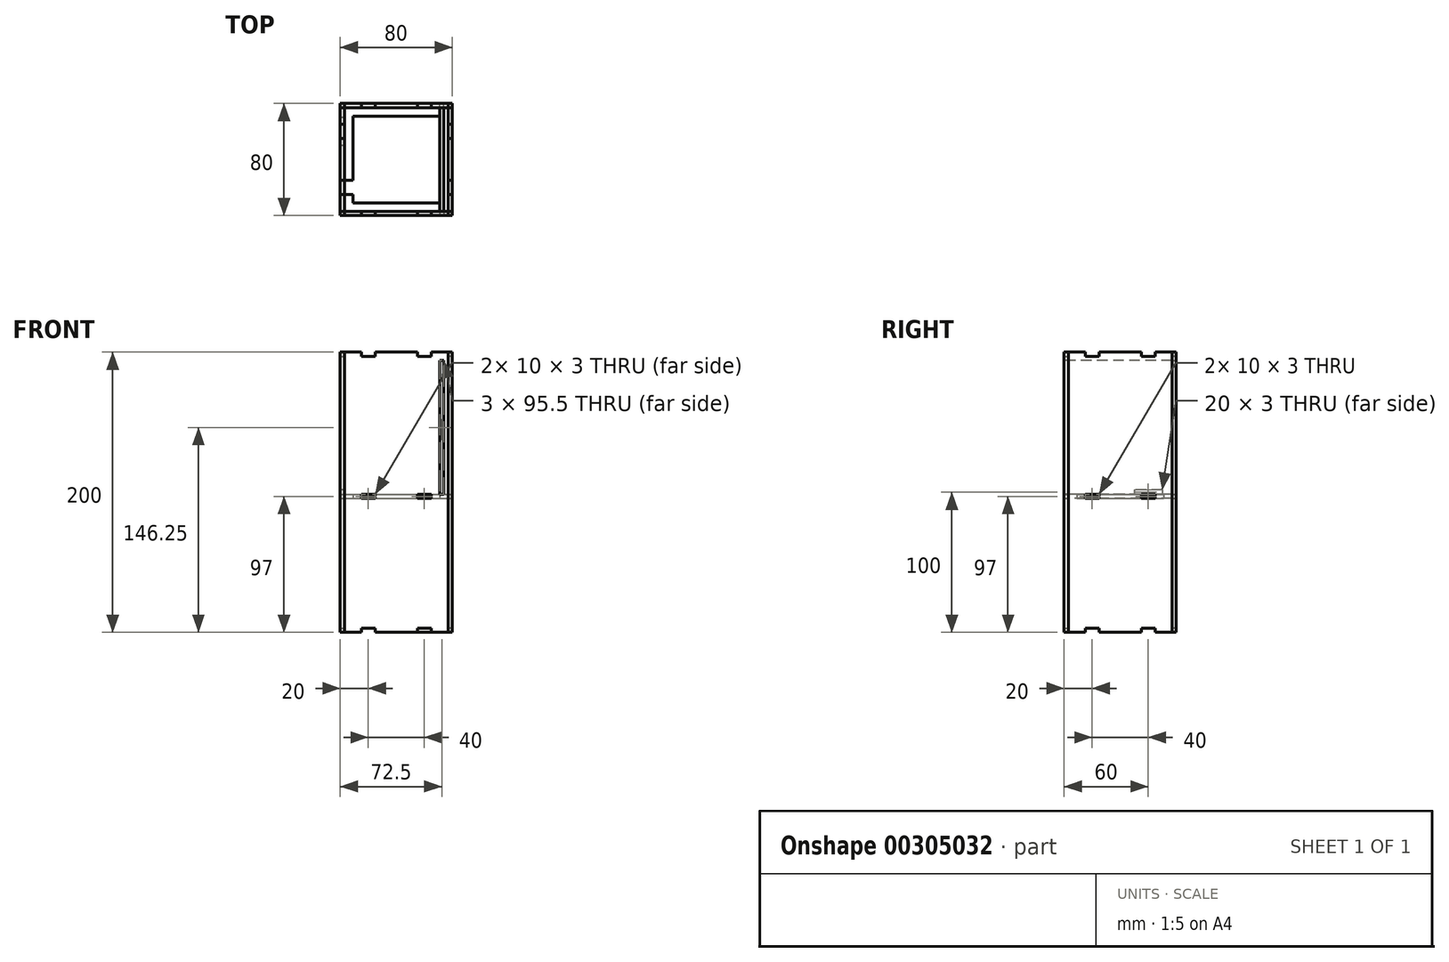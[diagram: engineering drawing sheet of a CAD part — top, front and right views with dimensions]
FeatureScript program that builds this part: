
annotation { "Feature Type Name" : "Feature", "Feature Type Description" : "" }
export const myFeature = defineFeature(function(context is Context, id is Id, definition is map)
    precondition{}
    {
        {
            assignVariable(context, id + "F0", {"name" : "WT", "anyValue" : 3});
        }
        {
            assignVariable(context, id + "F1", {"name" : "BW", "anyValue" : 80});
        }
        {
            assignVariable(context, id + "F2", {"name" : "BL", "anyValue" : 200});
        }
        {
            var Q0;
            Q0=qCreatedBy(makeId("Top.planeOp"),FACE);
            var sketch = newSketch(context, id + "F3", { "sketchPlane" : qUnion([Q0])});
            skLineSegment(sketch, "E0.bottom", {"start": v(-40, 40) * mm, "end": v(40, 40) * mm});
            skLineSegment(sketch, "E0.top", {"start": v(-40, -40) * mm, "end": v(40, -40) * mm});
            skLineSegment(sketch, "E0.left", {"start": v(-40, 40) * mm, "end": v(-40, -40) * mm});
            skLineSegment(sketch, "E0.right", {"start": v(40, 40) * mm, "end": v(40, -40) * mm});
            skPoint(sketch, "E0.middle", {"position": v(0, 0) * mm});
            skLineSegment(sketch, "E1.bottom", {"start": v(-37, 37) * mm, "end": v(37, 37) * mm});
            skLineSegment(sketch, "E1.top", {"start": v(-37, -37) * mm, "end": v(37, -37) * mm});
            skLineSegment(sketch, "E1.left", {"start": v(-37, 37) * mm, "end": v(-37, -37) * mm});
            skLineSegment(sketch, "E1.right", {"start": v(37, 37) * mm, "end": v(37, -37) * mm});
            skCircle(sketch, "E2", {"center": v(0, 0) * mm, "radius": 25 * mm});
            skLineSegment(sketch, "E3", {"start": v(37, 0) * mm, "end": v(40, 0) * mm, "construction": true});
            skLineSegment(sketch, "E4", {"start": v(37, 0) * mm, "end": v(40, 40) * mm, "construction": true});
            skLineSegment(sketch, "E5", {"start": v(0, 37) * mm, "end": v(0, 40) * mm, "construction": true});
            skLineSegment(sketch, "E6", {"start": v(0, 37) * mm, "end": v(40, 40) * mm, "construction": true});
            skLineSegment(sketch, "E7.bottom", {"start": v(25, 40) * mm, "end": v(15, 40) * mm});
            skLineSegment(sketch, "E7.top", {"start": v(25, 37) * mm, "end": v(15, 37) * mm});
            skLineSegment(sketch, "E7.left", {"start": v(25, 40) * mm, "end": v(25, 37) * mm});
            skLineSegment(sketch, "E7.right", {"start": v(15, 40) * mm, "end": v(15, 37) * mm});
            skPoint(sketch, "E7.middle", {"position": v(20, 38.5) * mm});
            skLineSegment(sketch, "E8.bottom", {"start": v(40, 25) * mm, "end": v(37, 25) * mm});
            skLineSegment(sketch, "E8.top", {"start": v(40, 15) * mm, "end": v(37, 15) * mm});
            skLineSegment(sketch, "E8.left", {"start": v(40, 25) * mm, "end": v(40, 15) * mm});
            skLineSegment(sketch, "E8.right", {"start": v(37, 25) * mm, "end": v(37, 15) * mm});
            skPoint(sketch, "E8.middle", {"position": v(38.5, 20) * mm});
            skLineSegment(sketch, "E9.MirrorCS", {"start": v(40, -15) * mm, "end": v(37, -15) * mm});
            skLineSegment(sketch, "E10.MirrorCS", {"start": v(40, -25) * mm, "end": v(37, -25) * mm});
            skLineSegment(sketch, "E11.MirrorCS", {"start": v(-15, 40) * mm, "end": v(-15, 37) * mm});
            skLineSegment(sketch, "E12.MirrorCS", {"start": v(-25, 40) * mm, "end": v(-25, 37) * mm});
            skLineSegment(sketch, "E13.MirrorCS", {"start": v(-40, 25) * mm, "end": v(-37, 25) * mm});
            skLineSegment(sketch, "E14.MirrorCS", {"start": v(-40, 15) * mm, "end": v(-37, 15) * mm});
            skLineSegment(sketch, "E15.MirrorCS", {"start": v(-40, -15) * mm, "end": v(-37, -15) * mm});
            skLineSegment(sketch, "E16.MirrorCS", {"start": v(-40, -25) * mm, "end": v(-37, -25) * mm});
            skLineSegment(sketch, "E17.MirrorCS", {"start": v(15, -40) * mm, "end": v(15, -37) * mm});
            skLineSegment(sketch, "E18.MirrorCS", {"start": v(25, -40) * mm, "end": v(25, -37) * mm});
            skLineSegment(sketch, "E19.MirrorCS", {"start": v(-15, -40) * mm, "end": v(-15, -37) * mm});
            skLineSegment(sketch, "E20.MirrorCS", {"start": v(-25, -40) * mm, "end": v(-25, -37) * mm});
            skSolve(sketch);
        }
        {
            var Q0;
            Q0=qCreatedBy(makeId("Front.planeOp"),FACE);
            cPlane(context, id + "F4", {"entities" : qUnion([Q0]), "cplaneType" : CPlaneType.OFFSET, "offset" : getVariable(context, 'BW') / 2 * mm, "width" : 150 * mm, "height" : 150 * mm});
        }
        {
            var Q0;
            Q0=qCreatedBy(id+"F4.planeOp",FACE);
            var sketch = newSketch(context, id + "F5", { "sketchPlane" : qUnion([Q0])});
            skLineSegment(sketch, "E21.0", {"start": v(-40, 0) * mm, "end": v(40, 0) * mm});
            skLineSegment(sketch, "E22", {"start": v(-40, 0) * mm, "end": v(-40, 200) * mm});
            skLineSegment(sketch, "E23.MirrorCS", {"start": v(40, 0) * mm, "end": v(40, 200) * mm});
            skLineSegment(sketch, "E24", {"start": v(-40, 100) * mm, "end": v(40, 100) * mm, "construction": true});
            skLineSegment(sketch, "E25.MirrorCS", {"start": v(-40, 200) * mm, "end": v(40, 200) * mm});
            skLineSegment(sketch, "E26.bottom", {"start": v(-37, 197) * mm, "end": v(37, 197) * mm});
            skLineSegment(sketch, "E26.top", {"start": v(-37, 3) * mm, "end": v(37, 3) * mm});
            skLineSegment(sketch, "E26.left", {"start": v(-37, 197) * mm, "end": v(-37, 3) * mm});
            skLineSegment(sketch, "E26.right", {"start": v(37, 197) * mm, "end": v(37, 3) * mm});
            skPoint(sketch, "E26.middle", {"position": v(0, 100) * mm});
            skLineSegment(sketch, "E27", {"start": v(-40, 101.5) * mm, "end": v(-37, 101.5) * mm});
            skLineSegment(sketch, "E28", {"start": v(-40, 98.5) * mm, "end": v(-37, 98.5) * mm});
            skLineSegment(sketch, "E29", {"start": v(-37, 98.5) * mm, "end": v(-34, 98.5) * mm});
            skLineSegment(sketch, "E30", {"start": v(-34, 98.5) * mm, "end": v(-34, 194) * mm});
            skLineSegment(sketch, "E31", {"start": v(0, 100) * mm, "end": v(0, 148.42) * mm, "construction": true});
            skLineSegment(sketch, "E32", {"start": v(-31, 95.5) * mm, "end": v(-31, 194) * mm});
            skLineSegment(sketch, "E33", {"start": v(-34, 194) * mm, "end": v(-31, 194) * mm});
            skLineSegment(sketch, "E34", {"start": v(-31, 95.5) * mm, "end": v(-37, 95.5) * mm});
            skLineSegment(sketch, "E35.MirrorCS", {"start": v(31, 95.5) * mm, "end": v(31, 194) * mm});
            skLineSegment(sketch, "E36.MirrorCS", {"start": v(31, 95.5) * mm, "end": v(37, 95.5) * mm});
            skLineSegment(sketch, "E37.MirrorCS", {"start": v(34, 98.5) * mm, "end": v(34, 194) * mm});
            skLineSegment(sketch, "E38.MirrorCS", {"start": v(34, 194) * mm, "end": v(31, 194) * mm});
            skLineSegment(sketch, "E39.MirrorCS", {"start": v(37, 98.5) * mm, "end": v(34, 98.5) * mm});
            skLineSegment(sketch, "E40.MirrorCS", {"start": v(40, 98.5) * mm, "end": v(37, 98.5) * mm});
            skLineSegment(sketch, "E41.MirrorCS", {"start": v(40, 101.5) * mm, "end": v(37, 101.5) * mm});
            skLineSegment(sketch, "E42", {"start": v(-34, 98.5) * mm, "end": v(-31, 98.5) * mm});
            skLineSegment(sketch, "E43", {"start": v(34, 98.5) * mm, "end": v(31, 98.5) * mm});
            skSolve(sketch);
        }
        {
            var Q0;
            Q0=qCreatedBy(id+"F4.planeOp",FACE);
            var sketch = newSketch(context, id + "F6", { "sketchPlane" : qUnion([Q0])});
            skLineSegment(sketch, "E44.0", {"start": v(-40, 200) * mm, "end": v(40, 200) * mm});
            skLineSegment(sketch, "E45.0", {"start": v(40, 0) * mm, "end": v(40, 200) * mm});
            skLineSegment(sketch, "E46.0", {"start": v(-40, 0) * mm, "end": v(-40, 200) * mm});
            skLineSegment(sketch, "E47.0", {"start": v(-40, 0) * mm, "end": v(40, 0) * mm});
            skSolve(sketch);
        }
        {
            var Q0;
            Q0=qCreatedBy(makeId("Front.planeOp"),FACE);
            cPlane(context, id + "F7", {"entities" : qUnion([Q0]), "cplaneType" : CPlaneType.OFFSET, "offset" : (getVariable(context, 'BW') / 2) * mm, "oppositeDirection" : true, "width" : 150 * mm, "height" : 150 * mm});
        }
        {
            var Q0;
            Q0=qCreatedBy(id+"F7.planeOp",FACE);
            var sketch = newSketch(context, id + "F8", { "sketchPlane" : qUnion([Q0])});
            skLineSegment(sketch, "E48.0", {"start": v(-40, 0) * mm, "end": v(-40, 200) * mm});
            skLineSegment(sketch, "E49.0", {"start": v(-40, 200) * mm, "end": v(40, 200) * mm});
            skLineSegment(sketch, "E50.0", {"start": v(40, 0) * mm, "end": v(40, 200) * mm});
            skLineSegment(sketch, "E51.0", {"start": v(-40, 0) * mm, "end": v(40, 0) * mm});
            skLineSegment(sketch, "E52.0", {"start": v(-37, 197) * mm, "end": v(-37, 3) * mm});
            skLineSegment(sketch, "E53.0", {"start": v(37, 197) * mm, "end": v(37, 3) * mm});
            skLineSegment(sketch, "E54.0", {"start": v(-37, 197) * mm, "end": v(37, 197) * mm});
            skLineSegment(sketch, "E55.0", {"start": v(-37, 3) * mm, "end": v(37, 3) * mm});
            skSolve(sketch);
        }
        {
            var Q0;
            Q0=qCreatedBy(makeId("Top.planeOp"),FACE);
            cPlane(context, id + "F9", {"entities" : qUnion([Q0]), "cplaneType" : CPlaneType.OFFSET, "offset" : (getVariable(context, 'BL')) * mm, "width" : 150 * mm, "height" : 150 * mm});
        }
        {
            var Q0;
            Q0=qCreatedBy(id+"F9.planeOp",FACE);
            var sketch = newSketch(context, id + "F10", { "sketchPlane" : qUnion([Q0])});
            skLineSegment(sketch, "E56.0", {"start": v(-40, 40) * mm, "end": v(-40, -40) * mm});
            skLineSegment(sketch, "E57.0", {"start": v(-40, 40) * mm, "end": v(40, 40) * mm});
            skLineSegment(sketch, "E58.0", {"start": v(40, 40) * mm, "end": v(40, -40) * mm});
            skLineSegment(sketch, "E59.0", {"start": v(-40, -40) * mm, "end": v(40, -40) * mm});
            skLineSegment(sketch, "E60.0", {"start": v(-37, -37) * mm, "end": v(37, -37) * mm});
            skLineSegment(sketch, "E61.0", {"start": v(-37, 37) * mm, "end": v(-37, -37) * mm});
            skLineSegment(sketch, "E62.0", {"start": v(37, 37) * mm, "end": v(37, -37) * mm});
            skLineSegment(sketch, "E63.0", {"start": v(-37, 37) * mm, "end": v(37, 37) * mm});
            skLineSegment(sketch, "E64.0", {"start": v(40, -25) * mm, "end": v(37, -25) * mm});
            skLineSegment(sketch, "E65.0", {"start": v(40, -15) * mm, "end": v(37, -15) * mm});
            skLineSegment(sketch, "E65.1", {"start": v(25, -40) * mm, "end": v(25, -37) * mm});
            skLineSegment(sketch, "E65.2", {"start": v(15, -40) * mm, "end": v(15, -37) * mm});
            skLineSegment(sketch, "E65.3", {"start": v(-15, -40) * mm, "end": v(-15, -37) * mm});
            skLineSegment(sketch, "E65.4", {"start": v(-25, -40) * mm, "end": v(-25, -37) * mm});
            skLineSegment(sketch, "E65.5", {"start": v(-40, -25) * mm, "end": v(-37, -25) * mm});
            skLineSegment(sketch, "E65.6", {"start": v(-40, -15) * mm, "end": v(-37, -15) * mm});
            skLineSegment(sketch, "E65.7", {"start": v(-40, 15) * mm, "end": v(-37, 15) * mm});
            skLineSegment(sketch, "E65.8", {"start": v(-40, 25) * mm, "end": v(-37, 25) * mm});
            skLineSegment(sketch, "E65.9", {"start": v(-25, 40) * mm, "end": v(-25, 37) * mm});
            skLineSegment(sketch, "E65.10", {"start": v(-15, 40) * mm, "end": v(-15, 37) * mm});
            skLineSegment(sketch, "E65.11", {"start": v(15, 40) * mm, "end": v(15, 37) * mm});
            skLineSegment(sketch, "E65.12", {"start": v(25, 40) * mm, "end": v(25, 37) * mm});
            skLineSegment(sketch, "E65.13", {"start": v(40, 25) * mm, "end": v(37, 25) * mm});
            skLineSegment(sketch, "E65.14", {"start": v(40, 15) * mm, "end": v(37, 15) * mm});
            skCircle(sketch, "E66.0", {"center": v(0, 0) * mm, "radius": 25 * mm});
            skSolve(sketch);
        }
        {
            var Q0;
            Q0=qCreatedBy(makeId("Right.planeOp"),FACE);
            cPlane(context, id + "F11", {"entities" : qUnion([Q0]), "cplaneType" : CPlaneType.OFFSET, "offset" : (getVariable(context, 'BW') / 2) * mm, "width" : 150 * mm, "height" : 150 * mm});
        }
        {
            var Q0;
            Q0=qCreatedBy(id+"F11.planeOp",FACE);
            var sketch = newSketch(context, id + "F12", { "sketchPlane" : qUnion([Q0])});
            skLineSegment(sketch, "E67.0", {"start": v(-40, 0) * mm, "end": v(-40, 200) * mm});
            skLineSegment(sketch, "E68.0", {"start": v(40, 200) * mm, "end": v(-40, 200) * mm});
            skLineSegment(sketch, "E69.0", {"start": v(40, 0) * mm, "end": v(40, 200) * mm});
            skLineSegment(sketch, "E70.0", {"start": v(40, 0) * mm, "end": v(-40, 0) * mm});
            skSolve(sketch);
        }
        {
            var Q0;
            Q0=qCreatedBy(makeId("Right.planeOp"),FACE);
            cPlane(context, id + "F13", {"entities" : qUnion([Q0]), "cplaneType" : CPlaneType.OFFSET, "offset" : (getVariable(context, 'BW') / 2) * mm, "oppositeDirection" : true, "width" : 150 * mm, "height" : 150 * mm});
        }
        {
            var Q0;
            Q0=qCreatedBy(id+"F13.planeOp",FACE);
            var sketch = newSketch(context, id + "F14", { "sketchPlane" : qUnion([Q0])});
            skLineSegment(sketch, "E71.0", {"start": v(40, 0) * mm, "end": v(40, 200) * mm});
            skLineSegment(sketch, "E72.0", {"start": v(-40, 0) * mm, "end": v(-40, 200) * mm});
            skLineSegment(sketch, "E73.0", {"start": v(40, 200) * mm, "end": v(-40, 200) * mm});
            skLineSegment(sketch, "E74.0", {"start": v(40, 0) * mm, "end": v(-40, 0) * mm});
            skLineSegment(sketch, "E75", {"start": v(40, 100) * mm, "end": v(-40, 100) * mm, "construction": true});
            skLineSegment(sketch, "E76", {"start": v(0, 100) * mm, "end": v(0, 101.5) * mm, "construction": true});
            skPoint(sketch, "E76.endSnap0", {"position": v(0, 100) * mm});
            skLineSegment(sketch, "E77", {"start": v(0, 100) * mm, "end": v(0, 98.5) * mm, "construction": true});
            skLineSegment(sketch, "E78", {"start": v(0, 101.5) * mm, "end": v(40, 101.5) * mm, "construction": true});
            skLineSegment(sketch, "E79", {"start": v(40, 101.5) * mm, "end": v(0, 98.5) * mm, "construction": true});
            skLineSegment(sketch, "E80.bottom", {"start": v(30, 101.5) * mm, "end": v(10, 101.5) * mm});
            skLineSegment(sketch, "E80.top", {"start": v(30, 98.5) * mm, "end": v(10, 98.5) * mm});
            skLineSegment(sketch, "E80.left", {"start": v(30, 101.5) * mm, "end": v(30, 98.5) * mm});
            skLineSegment(sketch, "E80.right", {"start": v(10, 101.5) * mm, "end": v(10, 98.5) * mm});
            skPoint(sketch, "E80.middle", {"position": v(20, 100) * mm});
            skSolve(sketch);
        }
        {
            var Q0;
            Q0=makeQuery(id+"F5.imprint","IMPRINT",FACE,{"disambiguationData":[TD([[makeQuery(id+"F5.imprint","IMPRINT",EDGE,{"derivedFrom":sQuery(id+"F5.wireOp",EDGE,"E35.MirrorCS")}),-1.0]])]});
            extrude(context, id + "F15", {"entities" : qUnion([Q0]), "oppositeDirection" : true, "depth" : (getVariable(context, 'BW')) * mm});
        }
        {
            var Q0;
            Q0=sQuery(id+"F5.wireOp",EDGE,"E34");
            cPlane(context, id + "F16", {"entities" : qUnion([Q0]), "cplaneType" : CPlaneType.LINE_ANGLE, "offset" : 25 * mm, "angle" : 90 * degree, "width" : 150 * mm, "height" : 150 * mm});
        }
        {
            var Q0;
            Q0=qCreatedBy(id+"F16.planeOp",FACE);
            var sketch = newSketch(context, id + "F17", { "sketchPlane" : qUnion([Q0])});
            skLineSegment(sketch, "E81.0", {"start": v(-40, 40) * mm, "end": v(-40, -40) * mm});
            skLineSegment(sketch, "E82.0", {"start": v(-40, -40) * mm, "end": v(40, -40) * mm});
            skLineSegment(sketch, "E83.0", {"start": v(40, 40) * mm, "end": v(40, -40) * mm});
            skLineSegment(sketch, "E84.0", {"start": v(-40, 40) * mm, "end": v(40, 40) * mm});
            skLineSegment(sketch, "E85.bottom", {"start": v(-31, -31) * mm, "end": v(31, -31) * mm});
            skLineSegment(sketch, "E85.top", {"start": v(-31, 31) * mm, "end": v(31, 31) * mm});
            skLineSegment(sketch, "E85.left", {"start": v(-31, -31) * mm, "end": v(-31, 31) * mm});
            skLineSegment(sketch, "E85.right", {"start": v(31, -31) * mm, "end": v(31, 31) * mm});
            skPoint(sketch, "E85.middle", {"position": v(0, 0) * mm});
            skLineSegment(sketch, "E86", {"start": v(0, -31) * mm, "end": v(0, -40) * mm, "construction": true});
            skLineSegment(sketch, "E87", {"start": v(-31, 0) * mm, "end": v(-40, 0) * mm, "construction": true});
            skLineSegment(sketch, "E88", {"start": v(-31, 0) * mm, "end": v(-40, -40) * mm, "construction": true});
            skLineSegment(sketch, "E89", {"start": v(-40, -40) * mm, "end": v(0, -31) * mm, "construction": true});
            skLineSegment(sketch, "E90.bottom", {"start": v(-25, -40) * mm, "end": v(-15, -40) * mm, "construction": true});
            skLineSegment(sketch, "E90.top", {"start": v(-25, -31) * mm, "end": v(-15, -31) * mm, "construction": true});
            skLineSegment(sketch, "E90.left", {"start": v(-25, -40) * mm, "end": v(-25, -31) * mm});
            skLineSegment(sketch, "E90.right", {"start": v(-15, -40) * mm, "end": v(-15, -31) * mm});
            skPoint(sketch, "E90.middle", {"position": v(-20, -35.5) * mm});
            skLineSegment(sketch, "E91.bottom", {"start": v(-40, -25) * mm, "end": v(-31, -25) * mm});
            skLineSegment(sketch, "E91.top", {"start": v(-40, -15) * mm, "end": v(-31, -15) * mm});
            skLineSegment(sketch, "E91.left", {"start": v(-40, -25) * mm, "end": v(-40, -15) * mm});
            skLineSegment(sketch, "E91.right", {"start": v(-31, -25) * mm, "end": v(-31, -15) * mm});
            skPoint(sketch, "E91.middle", {"position": v(-35.5, -20) * mm});
            skLineSegment(sketch, "E92.MirrorCS", {"start": v(15, -40) * mm, "end": v(15, -31) * mm});
            skLineSegment(sketch, "E93.MirrorCS", {"start": v(25, -40) * mm, "end": v(25, -31) * mm});
            skLineSegment(sketch, "E94.MirrorCS", {"start": v(-40, 15) * mm, "end": v(-31, 15) * mm});
            skLineSegment(sketch, "E95.MirrorCS", {"start": v(-40, 25) * mm, "end": v(-31, 25) * mm});
            skLineSegment(sketch, "E96.MirrorCS", {"start": v(-15, 40) * mm, "end": v(-15, 31) * mm});
            skLineSegment(sketch, "E97.MirrorCS", {"start": v(-25, 40) * mm, "end": v(-25, 31) * mm});
            skLineSegment(sketch, "E98.MirrorCS", {"start": v(15, 40) * mm, "end": v(15, 31) * mm});
            skLineSegment(sketch, "E99.MirrorCS", {"start": v(25, 40) * mm, "end": v(25, 31) * mm});
            skLineSegment(sketch, "E100.MirrorCS", {"start": v(40, -25) * mm, "end": v(31, -25) * mm});
            skLineSegment(sketch, "E101.MirrorCS", {"start": v(40, -15) * mm, "end": v(31, -15) * mm});
            skLineSegment(sketch, "E102.MirrorCS", {"start": v(40, 15) * mm, "end": v(31, 15) * mm});
            skLineSegment(sketch, "E103.MirrorCS", {"start": v(40, 25) * mm, "end": v(31, 25) * mm});
            skLineSegment(sketch, "E104.0", {"start": v(-37, 37) * mm, "end": v(37, 37) * mm});
            skLineSegment(sketch, "E105.0", {"start": v(37, 37) * mm, "end": v(37, -37) * mm});
            skLineSegment(sketch, "E106.0", {"start": v(-37, -37) * mm, "end": v(37, -37) * mm});
            skLineSegment(sketch, "E107.0", {"start": v(-37, 37) * mm, "end": v(-37, -37) * mm});
            skSolve(sketch);
        }
        {
            var Q0;
            {var subQ0=sQuery(id+"F17.wireOp",EDGE,"E96.MirrorCS");var subQ1=sQuery(id+"F17.wireOp",EDGE,"E85.top");var subQ2=makeQuery(id+"F17.imprint","INTERSECT",VERTEX,{"derivedFrom":[subQ1,subQ0]});Q0=makeQuery(id+"F17.imprint","IMPRINT",FACE,{"disambiguationData":[TD([[makeQuery(id+"F17.imprint","IMPRINT",EDGE,{"disambiguationData":[TD([[subQ2,1.0]])],"derivedFrom":subQ1}),1.0]])]});}
            var Q1;
            {var subQ0=sQuery(id+"F17.wireOp",EDGE,"E96.MirrorCS");var subQ1=sQuery(id+"F17.wireOp",EDGE,"E84.0");var subQ2=makeQuery(id+"F17.imprint","INTERSECT",VERTEX,{"derivedFrom":[subQ1,subQ0]});Q1=makeQuery(id+"F17.imprint","IMPRINT",FACE,{"disambiguationData":[TD([[makeQuery(id+"F17.imprint","IMPRINT",EDGE,{"disambiguationData":[TD([[subQ2,1.0]])],"derivedFrom":subQ1}),-1.0]])]});}
            var Q2;
            {var subQ0=sQuery(id+"F17.wireOp",EDGE,"E96.MirrorCS");var subQ1=sQuery(id+"F17.wireOp",EDGE,"E85.top");var subQ2=makeQuery(id+"F17.imprint","INTERSECT",VERTEX,{"derivedFrom":[subQ1,subQ0]});Q2=makeQuery(id+"F17.imprint","IMPRINT",FACE,{"disambiguationData":[TD([[makeQuery(id+"F17.imprint","IMPRINT",EDGE,{"disambiguationData":[TD([[subQ2,-1.0]])],"derivedFrom":subQ1}),1.0]])]});}
            var Q3;
            {var subQ1=sQuery(id+"F17.wireOp",EDGE,"E85.left");var subQ5=sQuery(id+"F17.wireOp",EDGE,"E85.top");var subQ6=makeQuery(id+"F17.imprint","INTERSECT",VERTEX,{"derivedFrom":[subQ5,subQ1]});Q3=makeQuery(id+"F17.imprint","IMPRINT",FACE,{"disambiguationData":[TD([[makeQuery(id+"F17.imprint","IMPRINT",EDGE,{"disambiguationData":[TD([[subQ6,-1.0]])],"derivedFrom":subQ5}),1.0]])]});}
            var Q4;
            {var subQ0=sQuery(id+"F17.wireOp",EDGE,"E98.MirrorCS");var subQ1=sQuery(id+"F17.wireOp",EDGE,"E85.top");var subQ2=makeQuery(id+"F17.imprint","INTERSECT",VERTEX,{"derivedFrom":[subQ1,subQ0]});Q4=makeQuery(id+"F17.imprint","IMPRINT",FACE,{"disambiguationData":[TD([[makeQuery(id+"F17.imprint","IMPRINT",EDGE,{"disambiguationData":[TD([[subQ2,-1.0]])],"derivedFrom":subQ1}),1.0]])]});}
            var Q5;
            {var subQ0=sQuery(id+"F17.wireOp",EDGE,"E98.MirrorCS");var subQ1=sQuery(id+"F17.wireOp",EDGE,"E84.0");var subQ2=makeQuery(id+"F17.imprint","INTERSECT",VERTEX,{"derivedFrom":[subQ1,subQ0]});Q5=makeQuery(id+"F17.imprint","IMPRINT",FACE,{"disambiguationData":[TD([[makeQuery(id+"F17.imprint","IMPRINT",EDGE,{"disambiguationData":[TD([[subQ2,-1.0]])],"derivedFrom":subQ1}),-1.0]])]});}
            var Q6;
            {var subQ1=sQuery(id+"F17.wireOp",EDGE,"E85.right");var subQ5=sQuery(id+"F17.wireOp",EDGE,"E85.top");var subQ6=makeQuery(id+"F17.imprint","INTERSECT",VERTEX,{"derivedFrom":[subQ5,subQ1]});Q6=makeQuery(id+"F17.imprint","IMPRINT",FACE,{"disambiguationData":[TD([[makeQuery(id+"F17.imprint","IMPRINT",EDGE,{"disambiguationData":[TD([[subQ6,1.0]])],"derivedFrom":subQ5}),1.0]])]});}
            var Q7;
            {var subQ0=sQuery(id+"F17.wireOp",EDGE,"E102.MirrorCS");var subQ1=sQuery(id+"F17.wireOp",EDGE,"E85.right");var subQ2=makeQuery(id+"F17.imprint","INTERSECT",VERTEX,{"derivedFrom":[subQ1,subQ0]});Q7=makeQuery(id+"F17.imprint","IMPRINT",FACE,{"disambiguationData":[TD([[makeQuery(id+"F17.imprint","IMPRINT",EDGE,{"disambiguationData":[TD([[subQ2,-1.0]])],"derivedFrom":subQ1}),-1.0]])]});}
            var Q8;
            {var subQ0=sQuery(id+"F17.wireOp",EDGE,"E102.MirrorCS");var subQ1=sQuery(id+"F17.wireOp",EDGE,"E83.0");var subQ2=makeQuery(id+"F17.imprint","INTERSECT",VERTEX,{"derivedFrom":[subQ1,subQ0]});Q8=makeQuery(id+"F17.imprint","IMPRINT",FACE,{"disambiguationData":[TD([[makeQuery(id+"F17.imprint","IMPRINT",EDGE,{"disambiguationData":[TD([[subQ2,1.0]])],"derivedFrom":subQ1}),-1.0]])]});}
            var Q9;
            {var subQ0=sQuery(id+"F17.wireOp",EDGE,"E94.MirrorCS");var subQ1=sQuery(id+"F17.wireOp",EDGE,"E81.0");var subQ2=makeQuery(id+"F17.imprint","INTERSECT",VERTEX,{"derivedFrom":[subQ1,subQ0]});Q9=makeQuery(id+"F17.imprint","IMPRINT",FACE,{"disambiguationData":[TD([[makeQuery(id+"F17.imprint","IMPRINT",EDGE,{"disambiguationData":[TD([[subQ2,1.0]])],"derivedFrom":subQ1}),1.0]])]});}
            var Q10;
            {var subQ0=sQuery(id+"F17.wireOp",EDGE,"E94.MirrorCS");var subQ1=sQuery(id+"F17.wireOp",EDGE,"E85.left");var subQ2=makeQuery(id+"F17.imprint","INTERSECT",VERTEX,{"derivedFrom":[subQ1,subQ0]});Q10=makeQuery(id+"F17.imprint","IMPRINT",FACE,{"disambiguationData":[TD([[makeQuery(id+"F17.imprint","IMPRINT",EDGE,{"disambiguationData":[TD([[subQ2,-1.0]])],"derivedFrom":subQ1}),1.0]])]});}
            var Q11;
            {var subQ1=sQuery(id+"F17.wireOp",EDGE,"E85.left");var subQ3=sQuery(id+"F17.wireOp",EDGE,"E94.MirrorCS");var subQ4=makeQuery(id+"F17.imprint","INTERSECT",VERTEX,{"derivedFrom":[subQ1,subQ3]});Q11=makeQuery(id+"F17.imprint","IMPRINT",FACE,{"disambiguationData":[TD([[makeQuery(id+"F17.imprint","IMPRINT",EDGE,{"disambiguationData":[TD([[subQ4,1.0]])],"derivedFrom":subQ3}),-1.0]])]});}
            var Q12;
            {var subQ0=sQuery(id+"F17.wireOp",EDGE,"E101.MirrorCS");var subQ1=sQuery(id+"F17.wireOp",EDGE,"E85.right");var subQ2=makeQuery(id+"F17.imprint","INTERSECT",VERTEX,{"derivedFrom":[subQ1,subQ0]});Q12=makeQuery(id+"F17.imprint","IMPRINT",FACE,{"disambiguationData":[TD([[makeQuery(id+"F17.imprint","IMPRINT",EDGE,{"disambiguationData":[TD([[subQ2,-1.0]])],"derivedFrom":subQ1}),-1.0]])]});}
            var Q13;
            {var subQ0=sQuery(id+"F17.wireOp",EDGE,"E100.MirrorCS");var subQ1=sQuery(id+"F17.wireOp",EDGE,"E85.right");var subQ2=makeQuery(id+"F17.imprint","INTERSECT",VERTEX,{"derivedFrom":[subQ1,subQ0]});Q13=makeQuery(id+"F17.imprint","IMPRINT",FACE,{"disambiguationData":[TD([[makeQuery(id+"F17.imprint","IMPRINT",EDGE,{"disambiguationData":[TD([[subQ2,-1.0]])],"derivedFrom":subQ1}),-1.0]])]});}
            var Q14;
            {var subQ0=sQuery(id+"F17.wireOp",EDGE,"E100.MirrorCS");var subQ1=sQuery(id+"F17.wireOp",EDGE,"E83.0");var subQ2=makeQuery(id+"F17.imprint","INTERSECT",VERTEX,{"derivedFrom":[subQ1,subQ0]});Q14=makeQuery(id+"F17.imprint","IMPRINT",FACE,{"disambiguationData":[TD([[makeQuery(id+"F17.imprint","IMPRINT",EDGE,{"disambiguationData":[TD([[subQ2,1.0]])],"derivedFrom":subQ1}),-1.0]])]});}
            var Q15;
            {var subQ0=sQuery(id+"F17.wireOp",EDGE,"E91.right");Q15=makeQuery(id+"F17.imprint","IMPRINT",FACE,{"disambiguationData":[TD([[makeQuery(id+"F17.imprint","IMPRINT",EDGE,{"derivedFrom":subQ0}),1.0]])]});}
            var Q16;
            {var subQ0=sQuery(id+"F17.wireOp",EDGE,"E91.left");Q16=makeQuery(id+"F17.imprint","IMPRINT",FACE,{"disambiguationData":[TD([[makeQuery(id+"F17.imprint","IMPRINT",EDGE,{"derivedFrom":subQ0}),-1.0]])]});}
            var Q17;
            {var subQ0=sQuery(id+"F17.wireOp",EDGE,"E90.left");var subQ1=sQuery(id+"F17.wireOp",EDGE,"E85.bottom");var subQ2=makeQuery(id+"F17.imprint","INTERSECT",VERTEX,{"derivedFrom":[subQ1,subQ0]});Q17=makeQuery(id+"F17.imprint","IMPRINT",FACE,{"disambiguationData":[TD([[makeQuery(id+"F17.imprint","IMPRINT",EDGE,{"disambiguationData":[TD([[subQ2,-1.0]])],"derivedFrom":subQ1}),-1.0]])]});}
            var Q18;
            {var subQ0=sQuery(id+"F17.wireOp",EDGE,"E90.left");var subQ1=sQuery(id+"F17.wireOp",EDGE,"E82.0");var subQ2=makeQuery(id+"F17.imprint","INTERSECT",VERTEX,{"derivedFrom":[subQ1,subQ0]});Q18=makeQuery(id+"F17.imprint","IMPRINT",FACE,{"disambiguationData":[TD([[makeQuery(id+"F17.imprint","IMPRINT",EDGE,{"disambiguationData":[TD([[subQ2,-1.0]])],"derivedFrom":subQ1}),1.0]])]});}
            var Q19;
            {var subQ0=sQuery(id+"F17.wireOp",EDGE,"E92.MirrorCS");var subQ1=sQuery(id+"F17.wireOp",EDGE,"E82.0");var subQ2=makeQuery(id+"F17.imprint","INTERSECT",VERTEX,{"derivedFrom":[subQ1,subQ0]});Q19=makeQuery(id+"F17.imprint","IMPRINT",FACE,{"disambiguationData":[TD([[makeQuery(id+"F17.imprint","IMPRINT",EDGE,{"disambiguationData":[TD([[subQ2,-1.0]])],"derivedFrom":subQ1}),1.0]])]});}
            var Q20;
            {var subQ0=sQuery(id+"F17.wireOp",EDGE,"E92.MirrorCS");var subQ1=sQuery(id+"F17.wireOp",EDGE,"E85.bottom");var subQ2=makeQuery(id+"F17.imprint","INTERSECT",VERTEX,{"derivedFrom":[subQ1,subQ0]});Q20=makeQuery(id+"F17.imprint","IMPRINT",FACE,{"disambiguationData":[TD([[makeQuery(id+"F17.imprint","IMPRINT",EDGE,{"disambiguationData":[TD([[subQ2,-1.0]])],"derivedFrom":subQ1}),-1.0]])]});}
            var Q21;
            {var subQ0=sQuery(id+"F17.wireOp",EDGE,"E90.right");var subQ1=sQuery(id+"F17.wireOp",EDGE,"E85.bottom");var subQ2=makeQuery(id+"F17.imprint","INTERSECT",VERTEX,{"derivedFrom":[subQ1,subQ0]});Q21=makeQuery(id+"F17.imprint","IMPRINT",FACE,{"disambiguationData":[TD([[makeQuery(id+"F17.imprint","IMPRINT",EDGE,{"disambiguationData":[TD([[subQ2,-1.0]])],"derivedFrom":subQ1}),-1.0]])]});}
            var Q22;
            {var subQ1=sQuery(id+"F17.wireOp",EDGE,"E85.left");var subQ6=sQuery(id+"F17.wireOp",EDGE,"E85.bottom");var subQ10=makeQuery(id+"F17.imprint","INTERSECT",VERTEX,{"derivedFrom":[subQ6,subQ1]});Q22=makeQuery(id+"F17.imprint","IMPRINT",FACE,{"disambiguationData":[TD([[makeQuery(id+"F17.imprint","IMPRINT",EDGE,{"disambiguationData":[TD([[subQ10,-1.0]])],"derivedFrom":subQ6}),-1.0]])]});}
            var Q23;
            {var subQ1=sQuery(id+"F17.wireOp",EDGE,"E85.right");var subQ6=sQuery(id+"F17.wireOp",EDGE,"E85.bottom");var subQ10=makeQuery(id+"F17.imprint","INTERSECT",VERTEX,{"derivedFrom":[subQ6,subQ1]});Q23=makeQuery(id+"F17.imprint","IMPRINT",FACE,{"disambiguationData":[TD([[makeQuery(id+"F17.imprint","IMPRINT",EDGE,{"disambiguationData":[TD([[subQ10,1.0]])],"derivedFrom":subQ6}),-1.0]])]});}
            extrude(context, id + "F18", {"entities" : qUnion([Q0, Q1, Q2, Q3, Q4, Q5, Q6, Q7, Q8, Q9, Q10, Q11, Q12, Q13, Q14, Q15, Q16, Q17, Q18, Q19, Q20, Q21, Q22, Q23]), "depth" : (getVariable(context, 'WT')) * mm});
        }
        {
            var Q0;
            Q0=makeQuery(id+"F12.imprint","IMPRINT",FACE,{"disambiguationData":[TD([[makeQuery(id+"F12.imprint","IMPRINT",EDGE,{"derivedFrom":sQuery(id+"F12.wireOp",EDGE,"E67.0")}),-1.0]])]});
            extrude(context, id + "F19", {"entities" : qUnion([Q0]), "oppositeDirection" : true, "depth" : (getVariable(context, 'WT')) * mm});
        }
        {
            var Q0;
            {var subQ0=sQuery(id+"F17.wireOp",EDGE,"E83.0");Q0=makeQuery(id+"F18.opExtrude","SWEPT_FACE",FACE,{"disambiguationData":[OSD([subQ0]),TDD([makeQuery(id+"F17.imprint","IMPRINT",EDGE,{"disambiguationData":[TD([[makeQuery(id+"F17.imprint","INTERSECT",VERTEX,{"derivedFrom":[subQ0,sQuery(id+"F17.wireOp",EDGE,"E100.MirrorCS")]}),1.0]])],"derivedFrom":subQ0})])]});}
            var Q1;
            {var subQ0=sQuery(id+"F17.wireOp",EDGE,"E83.0");Q1=makeQuery(id+"F18.opExtrude","SWEPT_FACE",FACE,{"disambiguationData":[OSD([subQ0]),TDD([makeQuery(id+"F17.imprint","IMPRINT",EDGE,{"disambiguationData":[TD([[makeQuery(id+"F17.imprint","INTERSECT",VERTEX,{"derivedFrom":[subQ0,sQuery(id+"F17.wireOp",EDGE,"E102.MirrorCS")]}),1.0]])],"derivedFrom":subQ0})])]});}
            extrude(context, id + "F20", {"entities" : qUnion([Q0, Q1]), "operationType" : NewBodyOperationType.REMOVE, "oppositeDirection" : true, "depth" : (getVariable(context, 'WT')) * mm});
        }
        {
            var Q0;
            Q0=makeQuery(id+"F8.imprint","IMPRINT",FACE,{"disambiguationData":[TD([[makeQuery(id+"F8.imprint","IMPRINT",EDGE,{"derivedFrom":sQuery(id+"F8.wireOp",EDGE,"E52.0")}),1.0]])]});
            var Q1;
            Q1=makeQuery(id+"F8.imprint","IMPRINT",FACE,{"disambiguationData":[TD([[makeQuery(id+"F8.imprint","IMPRINT",EDGE,{"derivedFrom":sQuery(id+"F8.wireOp",EDGE,"E48.0")}),-1.0]])]});
            extrude(context, id + "F21", {"entities" : qUnion([Q0, Q1]), "depth" : (getVariable(context, 'WT')) * mm});
        }
        {
            var Q0;
            Q0=makeQuery(id+"F15.opExtrude","CAP_FACE",FACE,{"disambiguationData":[OSD([sQuery(id+"F5.wireOp",EDGE,"E35.MirrorCS"),sQuery(id+"F5.wireOp",EDGE,"E37.MirrorCS"),sQuery(id+"F5.wireOp",EDGE,"E38.MirrorCS"),sQuery(id+"F5.wireOp",EDGE,"E43")])],"isStart":false});
            var Q1;
            Q1=makeQuery(id+"F15.opExtrude","CAP_FACE",FACE,{"disambiguationData":[OSD([sQuery(id+"F5.wireOp",EDGE,"E30"),sQuery(id+"F5.wireOp",EDGE,"E32"),sQuery(id+"F5.wireOp",EDGE,"E33"),sQuery(id+"F5.wireOp",EDGE,"E42")])],"isStart":false});
            var Q2;
            {var subQ0=sQuery(id+"F17.wireOp",EDGE,"E84.0");Q2=makeQuery(id+"F18.opExtrude","SWEPT_FACE",FACE,{"disambiguationData":[OSD([subQ0]),TDD([makeQuery(id+"F17.imprint","IMPRINT",EDGE,{"disambiguationData":[TD([[makeQuery(id+"F17.imprint","INTERSECT",VERTEX,{"derivedFrom":[subQ0,sQuery(id+"F17.wireOp",EDGE,"E98.MirrorCS")]}),-1.0]])],"derivedFrom":subQ0})])]});}
            var Q3;
            {var subQ0=sQuery(id+"F17.wireOp",EDGE,"E84.0");Q3=makeQuery(id+"F18.opExtrude","SWEPT_FACE",FACE,{"disambiguationData":[OSD([subQ0]),TDD([makeQuery(id+"F17.imprint","IMPRINT",EDGE,{"disambiguationData":[TD([[makeQuery(id+"F17.imprint","INTERSECT",VERTEX,{"derivedFrom":[subQ0,sQuery(id+"F17.wireOp",EDGE,"E96.MirrorCS")]}),1.0]])],"derivedFrom":subQ0})])]});}
            extrude(context, id + "F22", {"entities" : qUnion([Q0, Q1, Q2, Q3]), "operationType" : NewBodyOperationType.REMOVE, "oppositeDirection" : true, "depth" : (getVariable(context, 'WT')) * mm});
        }
        {
            var Q0;
            Q0=makeQuery(id+"F14.imprint","IMPRINT",FACE,{"disambiguationData":[TD([[makeQuery(id+"F14.imprint","IMPRINT",EDGE,{"derivedFrom":sQuery(id+"F14.wireOp",EDGE,"E71.0")}),1.0]])]});
            extrude(context, id + "F23", {"entities" : qUnion([Q0]), "depth" : (getVariable(context, 'WT')) * mm});
        }
        {
            var Q0;
            Q0=makeQuery(id+"F6.imprint","IMPRINT",FACE,{"disambiguationData":[TD([[makeQuery(id+"F6.imprint","IMPRINT",EDGE,{"derivedFrom":sQuery(id+"F6.wireOp",EDGE,"E44.0")}),-1.0]])]});
            extrude(context, id + "F24", {"entities" : qUnion([Q0]), "oppositeDirection" : true, "depth" : (getVariable(context, 'WT')) * mm});
        }
        {
            var Q0;
            Q0=makeQuery(id+"F3.imprint","IMPRINT",FACE,{"disambiguationData":[TD([[makeQuery(id+"F3.imprint","IMPRINT",EDGE,{"derivedFrom":sQuery(id+"F3.wireOp",EDGE,"E2")}),-1.0]])]});
            var Q1;
            Q1=makeQuery(id+"F3.imprint","IMPRINT",FACE,{"disambiguationData":[TD([[makeQuery(id+"F3.imprint","IMPRINT",EDGE,{"derivedFrom":sQuery(id+"F3.wireOp",EDGE,"E7.bottom")}),1.0]])]});
            var Q2;
            {var subQ0=sQuery(id+"F3.wireOp",EDGE,"E11.MirrorCS");Q2=makeQuery(id+"F3.imprint","IMPRINT",FACE,{"disambiguationData":[TD([[makeQuery(id+"F3.imprint","IMPRINT",EDGE,{"derivedFrom":subQ0}),-1.0]])]});}
            var Q3;
            Q3=makeQuery(id+"F3.imprint","IMPRINT",FACE,{"disambiguationData":[TD([[makeQuery(id+"F3.imprint","IMPRINT",EDGE,{"derivedFrom":sQuery(id+"F3.wireOp",EDGE,"E8.bottom")}),1.0]])]});
            var Q4;
            {var subQ0=sQuery(id+"F3.wireOp",EDGE,"E9.MirrorCS");Q4=makeQuery(id+"F3.imprint","IMPRINT",FACE,{"disambiguationData":[TD([[makeQuery(id+"F3.imprint","IMPRINT",EDGE,{"derivedFrom":subQ0}),1.0]])]});}
            var Q5;
            {var subQ0=sQuery(id+"F3.wireOp",EDGE,"E17.MirrorCS");Q5=makeQuery(id+"F3.imprint","IMPRINT",FACE,{"disambiguationData":[TD([[makeQuery(id+"F3.imprint","IMPRINT",EDGE,{"derivedFrom":subQ0}),-1.0]])]});}
            var Q6;
            {var subQ0=sQuery(id+"F3.wireOp",EDGE,"E19.MirrorCS");Q6=makeQuery(id+"F3.imprint","IMPRINT",FACE,{"disambiguationData":[TD([[makeQuery(id+"F3.imprint","IMPRINT",EDGE,{"derivedFrom":subQ0}),1.0]])]});}
            var Q7;
            {var subQ0=sQuery(id+"F3.wireOp",EDGE,"E15.MirrorCS");Q7=makeQuery(id+"F3.imprint","IMPRINT",FACE,{"disambiguationData":[TD([[makeQuery(id+"F3.imprint","IMPRINT",EDGE,{"derivedFrom":subQ0}),-1.0]])]});}
            var Q8;
            {var subQ0=sQuery(id+"F3.wireOp",EDGE,"E13.MirrorCS");Q8=makeQuery(id+"F3.imprint","IMPRINT",FACE,{"disambiguationData":[TD([[makeQuery(id+"F3.imprint","IMPRINT",EDGE,{"derivedFrom":subQ0}),-1.0]])]});}
            var Q9;
            Q9=makeQuery(id+"F3.imprint","IMPRINT",FACE,{"disambiguationData":[TD([[makeQuery(id+"F3.imprint","IMPRINT",EDGE,{"derivedFrom":sQuery(id+"F3.wireOp",EDGE,"E2")}),1.0]])]});
            extrude(context, id + "F25", {"entities" : qUnion([Q0, Q1, Q2, Q3, Q4, Q5, Q6, Q7, Q8, Q9]), "depth" : (getVariable(context, 'WT')) * mm});
        }
        {
            var Q0;
            Q0=makeQuery(id+"F25.opExtrude","CAP_FACE",FACE,{"disambiguationData":[OSD([sQuery(id+"F3.wireOp",EDGE,"E0.bottom"),sQuery(id+"F3.wireOp",EDGE,"E0.top"),sQuery(id+"F3.wireOp",EDGE,"E0.left"),sQuery(id+"F3.wireOp",EDGE,"E0.right"),sQuery(id+"F3.wireOp",EDGE,"E1.bottom"),sQuery(id+"F3.wireOp",EDGE,"E1.top"),sQuery(id+"F3.wireOp",EDGE,"E1.left"),sQuery(id+"F3.wireOp",EDGE,"E1.right"),sQuery(id+"F3.wireOp",EDGE,"E2"),sQuery(id+"F3.wireOp",EDGE,"E7.bottom"),sQuery(id+"F3.wireOp",EDGE,"E7.left"),sQuery(id+"F3.wireOp",EDGE,"E7.right"),sQuery(id+"F3.wireOp",EDGE,"E8.bottom"),sQuery(id+"F3.wireOp",EDGE,"E8.top"),sQuery(id+"F3.wireOp",EDGE,"E8.left"),sQuery(id+"F3.wireOp",EDGE,"E9.MirrorCS"),sQuery(id+"F3.wireOp",EDGE,"E10.MirrorCS"),sQuery(id+"F3.wireOp",EDGE,"E11.MirrorCS"),sQuery(id+"F3.wireOp",EDGE,"E12.MirrorCS"),sQuery(id+"F3.wireOp",EDGE,"E13.MirrorCS"),sQuery(id+"F3.wireOp",EDGE,"E14.MirrorCS"),sQuery(id+"F3.wireOp",EDGE,"E15.MirrorCS"),sQuery(id+"F3.wireOp",EDGE,"E16.MirrorCS"),sQuery(id+"F3.wireOp",EDGE,"E17.MirrorCS"),sQuery(id+"F3.wireOp",EDGE,"E18.MirrorCS"),sQuery(id+"F3.wireOp",EDGE,"E19.MirrorCS"),sQuery(id+"F3.wireOp",EDGE,"E20.MirrorCS")])],"isStart":true});
            extrude(context, id + "F26", {"entities" : qUnion([Q0]), "operationType" : NewBodyOperationType.REMOVE, "oppositeDirection" : true, "depth" : (getVariable(context, 'WT')) * mm});
        }
        {
            var Q0;
            {var subQ0=sQuery(id+"F10.wireOp",EDGE,"E61.0");var subQ1=sQuery(id+"F10.wireOp",EDGE,"E60.0");var subQ2=makeQuery(id+"F10.imprint","INTERSECT",VERTEX,{"derivedFrom":[subQ1,subQ0]});Q0=makeQuery(id+"F10.imprint","IMPRINT",FACE,{"disambiguationData":[TD([[makeQuery(id+"F10.imprint","IMPRINT",EDGE,{"disambiguationData":[TD([[subQ2,-1.0]])],"derivedFrom":subQ1}),1.0]])]});}
            var Q1;
            {var subQ0=sQuery(id+"F10.wireOp",EDGE,"E64.0");Q1=makeQuery(id+"F10.imprint","IMPRINT",FACE,{"disambiguationData":[TD([[makeQuery(id+"F10.imprint","IMPRINT",EDGE,{"derivedFrom":subQ0}),-1.0]])]});}
            var Q2;
            {var subQ0=sQuery(id+"F10.wireOp",EDGE,"E65.1");Q2=makeQuery(id+"F10.imprint","IMPRINT",FACE,{"disambiguationData":[TD([[makeQuery(id+"F10.imprint","IMPRINT",EDGE,{"derivedFrom":subQ0}),1.0]])]});}
            var Q3;
            {var subQ0=sQuery(id+"F10.wireOp",EDGE,"E65.3");Q3=makeQuery(id+"F10.imprint","IMPRINT",FACE,{"disambiguationData":[TD([[makeQuery(id+"F10.imprint","IMPRINT",EDGE,{"derivedFrom":subQ0}),1.0]])]});}
            var Q4;
            {var subQ0=sQuery(id+"F10.wireOp",EDGE,"E65.5");Q4=makeQuery(id+"F10.imprint","IMPRINT",FACE,{"disambiguationData":[TD([[makeQuery(id+"F10.imprint","IMPRINT",EDGE,{"derivedFrom":subQ0}),1.0]])]});}
            var Q5;
            {var subQ0=sQuery(id+"F10.wireOp",EDGE,"E65.7");Q5=makeQuery(id+"F10.imprint","IMPRINT",FACE,{"disambiguationData":[TD([[makeQuery(id+"F10.imprint","IMPRINT",EDGE,{"derivedFrom":subQ0}),1.0]])]});}
            var Q6;
            {var subQ0=sQuery(id+"F10.wireOp",EDGE,"E65.9");Q6=makeQuery(id+"F10.imprint","IMPRINT",FACE,{"disambiguationData":[TD([[makeQuery(id+"F10.imprint","IMPRINT",EDGE,{"derivedFrom":subQ0}),1.0]])]});}
            var Q7;
            {var subQ0=sQuery(id+"F10.wireOp",EDGE,"E65.11");Q7=makeQuery(id+"F10.imprint","IMPRINT",FACE,{"disambiguationData":[TD([[makeQuery(id+"F10.imprint","IMPRINT",EDGE,{"derivedFrom":subQ0}),1.0]])]});}
            var Q8;
            {var subQ0=sQuery(id+"F10.wireOp",EDGE,"E65.13");Q8=makeQuery(id+"F10.imprint","IMPRINT",FACE,{"disambiguationData":[TD([[makeQuery(id+"F10.imprint","IMPRINT",EDGE,{"derivedFrom":subQ0}),1.0]])]});}
            extrude(context, id + "F27", {"entities" : qUnion([Q0, Q1, Q2, Q3, Q4, Q5, Q6, Q7, Q8]), "oppositeDirection" : true, "depth" : (getVariable(context, 'WT')) * mm});
        }
        {
            var Q0;
            Q0=makeQuery(id+"F27.opExtrude","CAP_FACE",FACE,{"disambiguationData":[OSD([sQuery(id+"F10.wireOp",EDGE,"E56.0"),sQuery(id+"F10.wireOp",EDGE,"E57.0"),sQuery(id+"F10.wireOp",EDGE,"E58.0"),sQuery(id+"F10.wireOp",EDGE,"E59.0"),sQuery(id+"F10.wireOp",EDGE,"E60.0"),sQuery(id+"F10.wireOp",EDGE,"E61.0"),sQuery(id+"F10.wireOp",EDGE,"E62.0"),sQuery(id+"F10.wireOp",EDGE,"E63.0"),sQuery(id+"F10.wireOp",EDGE,"E64.0"),sQuery(id+"F10.wireOp",EDGE,"E65.0"),sQuery(id+"F10.wireOp",EDGE,"E65.1"),sQuery(id+"F10.wireOp",EDGE,"E65.2"),sQuery(id+"F10.wireOp",EDGE,"E65.3"),sQuery(id+"F10.wireOp",EDGE,"E65.4"),sQuery(id+"F10.wireOp",EDGE,"E65.5"),sQuery(id+"F10.wireOp",EDGE,"E65.6"),sQuery(id+"F10.wireOp",EDGE,"E65.7"),sQuery(id+"F10.wireOp",EDGE,"E65.8"),sQuery(id+"F10.wireOp",EDGE,"E65.9"),sQuery(id+"F10.wireOp",EDGE,"E65.10"),sQuery(id+"F10.wireOp",EDGE,"E65.11"),sQuery(id+"F10.wireOp",EDGE,"E65.12"),sQuery(id+"F10.wireOp",EDGE,"E65.13"),sQuery(id+"F10.wireOp",EDGE,"E65.14")])],"isStart":true});
            extrude(context, id + "F28", {"entities" : qUnion([Q0]), "operationType" : NewBodyOperationType.REMOVE, "oppositeDirection" : true, "depth" : (getVariable(context, 'WT')) * mm});
        }
    });
